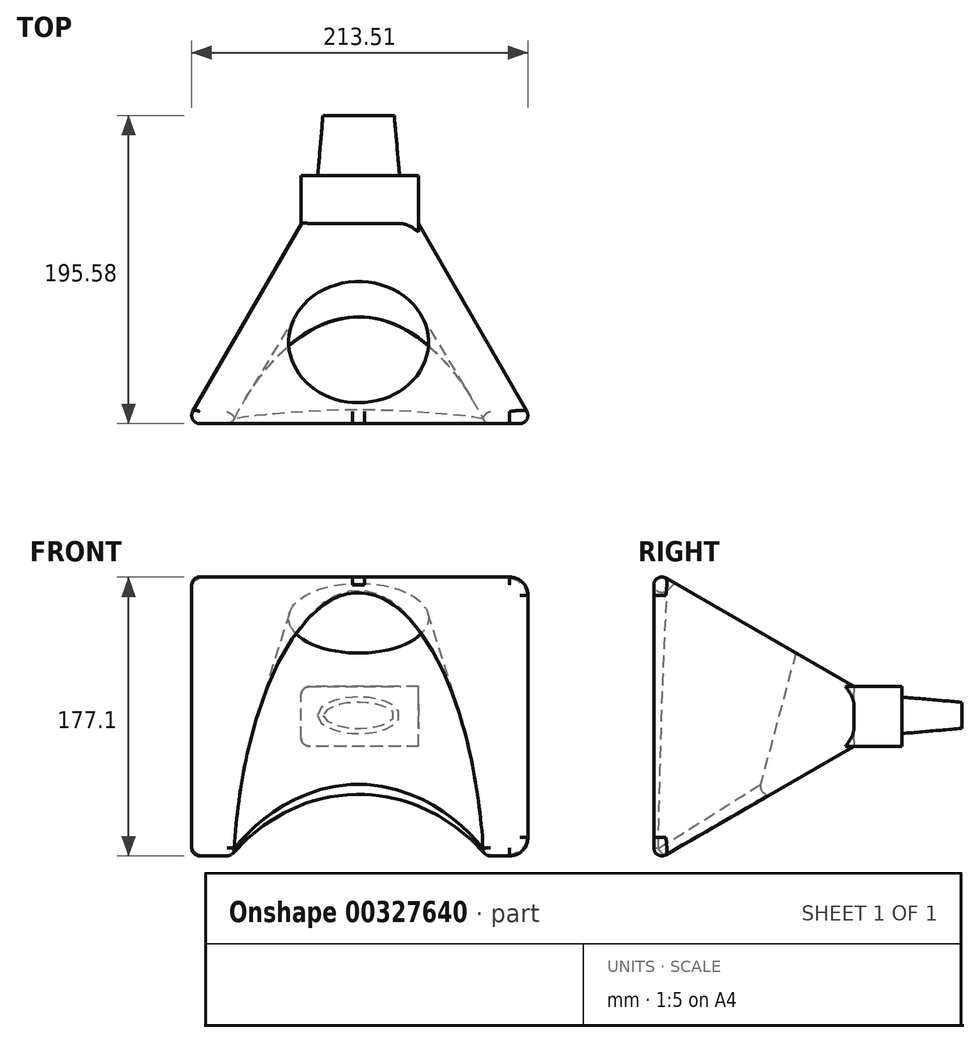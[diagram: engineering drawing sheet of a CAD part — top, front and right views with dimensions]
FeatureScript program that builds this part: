
annotation { "Feature Type Name" : "Feature", "Feature Type Description" : "" }
export const myFeature = defineFeature(function(context is Context, id is Id, definition is map)
    precondition{}
    {
        {
            var Q0;
            Q0=qCreatedBy(makeId("Front.planeOp"),FACE);
            var sketch = newSketch(context, id + "F0", { "sketchPlane" : qUnion([Q0])});
            skLineSegment(sketch, "E0.bottom", {"start": v(37.89, 3.86) * mm, "end": v(-36.42, 3.86) * mm});
            skLineSegment(sketch, "E0.top", {"start": v(37.89, 41.75) * mm, "end": v(-36.42, 41.75) * mm});
            skLineSegment(sketch, "E0.left", {"start": v(37.89, 3.86) * mm, "end": v(37.89, 41.75) * mm});
            skLineSegment(sketch, "E0.right", {"start": v(-36.42, 3.86) * mm, "end": v(-36.42, 41.75) * mm});
            skPoint(sketch, "E0.middle", {"position": v(0.74, 22.8) * mm});
            skSolve(sketch);
        }
        {
            var Q0;
            Q0 = qSketchRegion(id + "F0", true);
            extrude(context, id + "F1", {"entities" : qUnion([Q0]), "depth" : 127 * mm, "hasDraft" : true, "draftAngle" : 30 * degree});
        }
        {
            var Q0;
            Q0=makeQuery(id+"F1.opExtrude","SWEPT_FACE",FACE,{"disambiguationData":[OSD([sQuery(id+"F0.wireOp",EDGE,"E0.top")])]});
            var sketch = newSketch(context, id + "F2", { "sketchPlane" : qUnion([Q0])});
            skCircle(sketch, "E1", {"center": v(0, -107.82) * mm, "radius": 37.61 * mm});
            skSolve(sketch);
        }
        {
            var Q0;
            Q0 = qSketchRegion(id + "F2", true);
            extrude(context, id + "F3", {"entities" : qUnion([Q0]), "operationType" : NewBodyOperationType.ADD, "depth" : 25.4 * mm});
        }
        {
            var Q0;
            Q0=makeQuery(id+"F3.opExtrude","CAP_FACE",FACE,{"disambiguationData":[OSD([sQuery(id+"F2.wireOp",EDGE,"E1")])],"isStart":false});
            extrude(context, id + "F4", {"entities" : qUnion([Q0]), "operationType" : NewBodyOperationType.REMOVE, "oppositeDirection" : true, "depth" : 1422.4 * mm, "hasDraft" : true, "draftAngle" : 15 * degree, "offsetDistance" : 25.4 * mm});
        }
        {
            var Q0;
            Q0=makeQuery(id+"F0.imprint","IMPRINT",FACE,{"disambiguationData":[TD([[makeQuery(id+"F0.imprint","IMPRINT",EDGE,{"derivedFrom":sQuery(id+"F0.wireOp",EDGE,"E0.bottom")}),-1.0]])]});
            extrude(context, id + "F5", {"entities" : qUnion([Q0]), "operationType" : NewBodyOperationType.ADD, "oppositeDirection" : true, "depth" : 30.48 * mm});
        }
        {
            var Q0;
            Q0=makeQuery(id+"F1.opExtrude","SWEPT_EDGE",EDGE,{"disambiguationData":[OSD([sQuery(id+"F0.wireOp",EDGE,"E0.top"),sQuery(id+"F0.wireOp",EDGE,"E0.right")])]});
            var Q1;
            Q1=makeQuery(id+"F5.opExtrude","SWEPT_EDGE",EDGE,{"disambiguationData":[OSD([sQuery(id+"F0.wireOp",EDGE,"E0.top"),sQuery(id+"F0.wireOp",EDGE,"E0.right")])]});
            fillet(context, id + "F6", {"entities" : qUnion([Q0, Q1]), "radius" : 5.08 * mm, "tangentPropagation" : true, "allowEdgeOverflow" : false});
        }
        {
            var Q0;
            Q0=makeQuery(id+"F5.opExtrude","SWEPT_EDGE",EDGE,{"disambiguationData":[OSD([sQuery(id+"F0.wireOp",EDGE,"E0.bottom"),sQuery(id+"F0.wireOp",EDGE,"E0.right")])]});
            var Q1;
            Q1=makeQuery(id+"F1.opExtrude","SWEPT_EDGE",EDGE,{"disambiguationData":[OSD([sQuery(id+"F0.wireOp",EDGE,"E0.bottom"),sQuery(id+"F0.wireOp",EDGE,"E0.right")])]});
            fillet(context, id + "F7", {"entities" : qUnion([Q0, Q1]), "radius" : 5.08 * mm, "tangentPropagation" : true, "allowEdgeOverflow" : false});
        }
        {
            var Q0;
            Q0=makeQuery(id+"F5.opExtrude","CAP_FACE",FACE,{"disambiguationData":[OSD([sQuery(id+"F0.wireOp",EDGE,"E0.bottom"),sQuery(id+"F0.wireOp",EDGE,"E0.top"),sQuery(id+"F0.wireOp",EDGE,"E0.left"),sQuery(id+"F0.wireOp",EDGE,"E0.right")])],"isStart":false});
            var sketch = newSketch(context, id + "F8", { "sketchPlane" : qUnion([Q0])});
            skEllipse(sketch, "E2", {"center": v(0, 23.54) * mm, "majorRadius": 25.98 * mm, "minorRadius": 11.61 * mm, "majorAxis": v(-1, 0)});
            skSolve(sketch);
        }
        {
            var Q0;
            Q0 = qSketchRegion(id + "F8", true);
            extrude(context, id + "F9", {"entities" : qUnion([Q0]), "operationType" : NewBodyOperationType.ADD, "depth" : 38.1 * mm, "hasDraft" : true, "draftAngle" : 5 * degree, "draftPullDirection" : true});
        }
        {
            var Q0;
            Q0=makeQuery(id+"F1.opExtrude","SWEPT_EDGE",EDGE,{"disambiguationData":[OSD([sQuery(id+"F0.wireOp",EDGE,"E0.bottom"),sQuery(id+"F0.wireOp",EDGE,"E0.left")])]});
            var Q1;
            Q1=makeQuery(id+"F1.opExtrude","SWEPT_EDGE",EDGE,{"disambiguationData":[OSD([sQuery(id+"F0.wireOp",EDGE,"E0.top"),sQuery(id+"F0.wireOp",EDGE,"E0.left")])]});
            fillet(context, id + "F10", {"entities" : qUnion([Q0, Q1]), "radius" : 12.7 * mm, "tangentPropagation" : true, "allowEdgeOverflow" : false});
        }
        {
            var Q0;
            Q0=makeQuery(id+"F4.boolean.opBoolean","INTERSECT",EDGE,{"derivedFrom":[makeQuery(id+"F1.opExtrude","CAP_FACE",FACE,{"disambiguationData":[OSD([sQuery(id+"F0.wireOp",EDGE,"E0.bottom"),sQuery(id+"F0.wireOp",EDGE,"E0.top"),sQuery(id+"F0.wireOp",EDGE,"E0.left"),sQuery(id+"F0.wireOp",EDGE,"E0.right")])],"isStart":false}),makeQuery(id+"F4.opExtrude","SWEPT_FACE",FACE,{"disambiguationData":[OSD([sQuery(id+"F2.wireOp",EDGE,"E1")])]})]});
            fillet(context, id + "F11", {"entities" : qUnion([Q0]), "radius" : 5.08 * mm, "tangentPropagation" : true, "allowEdgeOverflow" : false});
        }
        {
            var Q0;
            Q0=makeQuery(id+"F4.boolean.opBoolean","INTERSECT",EDGE,{"derivedFrom":[makeQuery(id+"F1.opExtrude","SWEPT_FACE",FACE,{"disambiguationData":[OSD([sQuery(id+"F0.wireOp",EDGE,"E0.bottom")])]}),makeQuery(id+"F4.opExtrude","SWEPT_FACE",FACE,{"disambiguationData":[OSD([sQuery(id+"F2.wireOp",EDGE,"E1")])]})]});
            fillet(context, id + "F12", {"entities" : qUnion([Q0]), "radius" : 5.08 * mm, "tangentPropagation" : true, "allowEdgeOverflow" : false});
        }
    });
